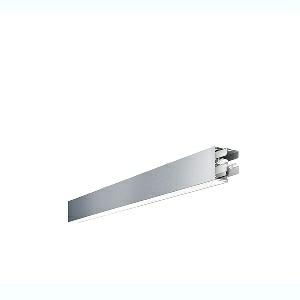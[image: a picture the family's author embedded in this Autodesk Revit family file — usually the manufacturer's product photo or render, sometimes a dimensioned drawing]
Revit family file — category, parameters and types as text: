
# Revit family: dotoo_line_-_dla_1500_840_d_mid_00807953_f3ed
name_source: partatom
category: Lighting Fixtures
units: mm (PartAtom-declared; Revit-internal decimal feet)

## family parameters
Cut with Voids When Loaded = No
Host = Face
Light Source = No
Part Type = Normal
Room Calculation Point = No
Round Connector Dimension = Use Diameter
Shared = No

## types (1)
- DOTOO.line - DLA 1500/840/D MID (1 x LED, 1350 lm, 4000K)
    Apparent Load = 13 VA
    Approval mark = CE
    CIE Flux Codes = 67 91 98 100 100
    Color Rendering = 80-89
    Color Temperature = 4000K
    Control Gear = Electronic ballast
    Default Elevation = 1800 mm
    Description = DLA 1500/840/D|Surface-mounted luminaire.|light source: LED|work equipment: Adjustable electronic ballast, digital DALI|connected load: 220-240 V, 50/60 Hz|Power consumption: approx. 13 W|luminous flux: 1350 lm|luminous efficacy: 103 lm/W|light distribution: Direct|colour temperature: Cold white, ca. 4000 K|class of protection: I|technology: Continuously dimmable|mains lead: Connector|glare control: Prism aperture|special features: DALI Load 1x, TouchDIM - dimming via standard switch, Through-wired, up to 18 m on one mains connection, Flicker-free, Suitable as emergency lighting, Mechanical and electrical connection of the individual modules without tools|
    Frequency = 50 Hz
    Height = 110 mm
    Lamp = 1 x LED
    Lamp Light Flux = 1350 lm
    Lamp count = 1
    Length = 1122 mm
    Luminous efficacy = 104 lm/W
    Manufacturer = Waldmann
    ModVariant = No
    Model = 00807953
    Mounting Place = Ceiling
    Mounting Type = Surface mounted
    Number of Poles = 1
    OnlyDefault = Yes
    Power Factor = 1
    Product Name = DOTOO.line - DLA 1500/840/D MID
    Product group = Ceiling mounted luminaire
    ProductGroupID = 3
    Protection Class = Protection class I
    Protection Degree = IP 40
    RLX_Detail_Level = 1
    RLX_Emergency_Light_Flux = 0 lm
    RLX_Emergency_Type = 0
    RLX_Emergency_Type_DB = No
    RlxData = <blob elided: 18125 chars, md5=7366cd7b>
    Socket = socket
    Standby Power = 0 W
    System Light Flux = 1350 lm
    System Power = 13 W
    Type Comments = Product without accessories
    Type Image = 114373000-00807950.jpg
    URL = http://relux.com
    VarID = ---
    Voltage = 230 V
    Voltage Range = 220-240 V
    Weight = 0.00 kg
    Width = 60 mm  [stored 0.19685 ft]

note: [stored X ft] marks values corroborated as IEEE doubles in the binary element streams (Revit-internal decimal feet)

## geometry (parser evidence)
native form markers: Blend x4, Sweep x10
no freeform markers — native parametric forms only
